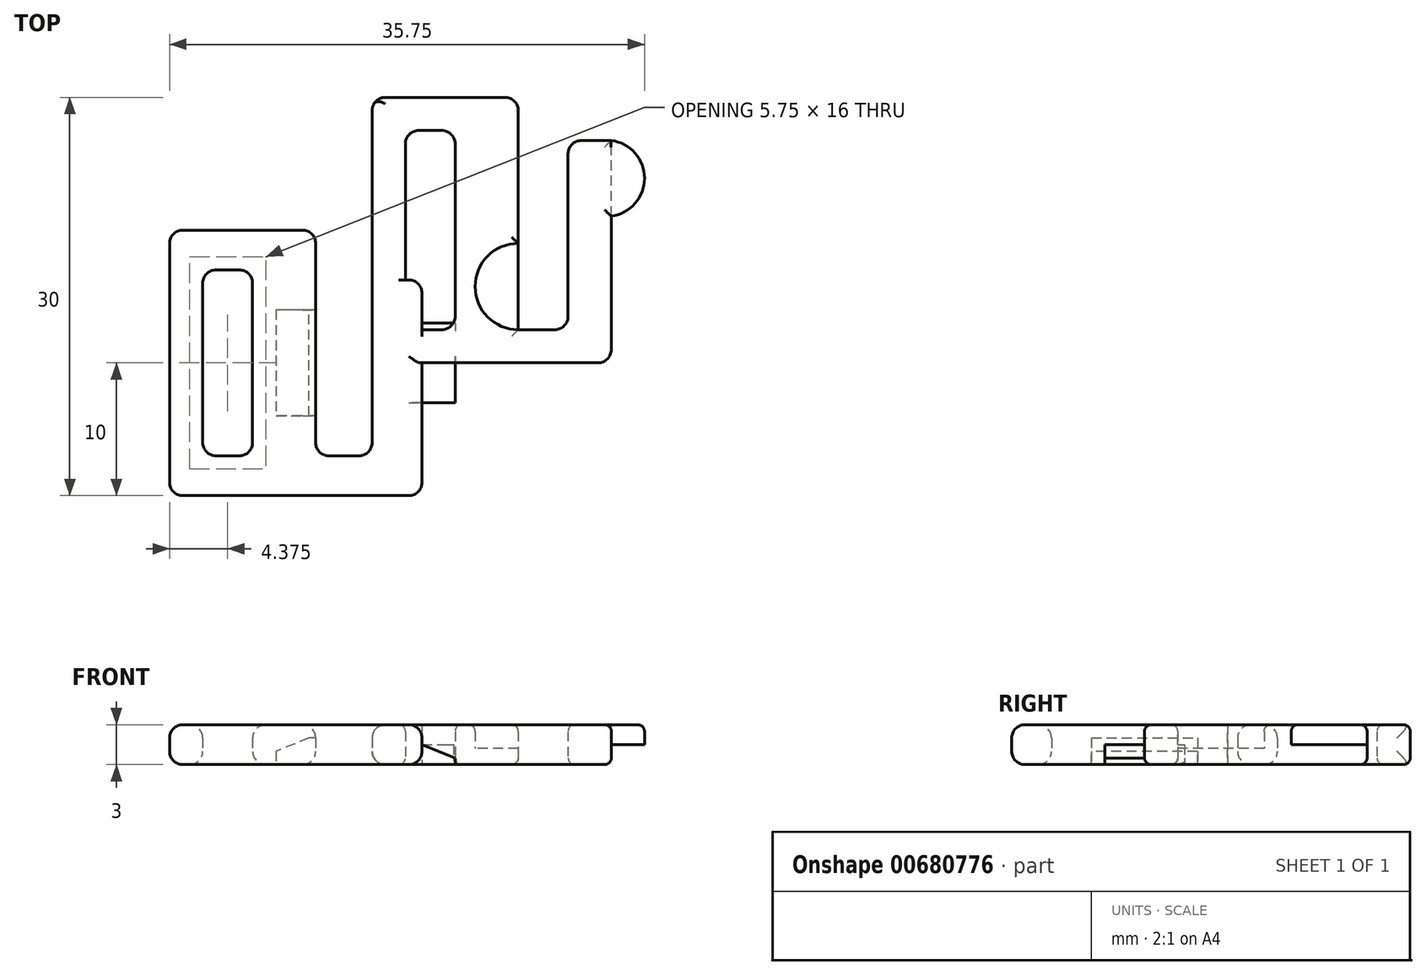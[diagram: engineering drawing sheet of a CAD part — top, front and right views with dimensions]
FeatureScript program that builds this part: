
annotation { "Feature Type Name" : "Feature", "Feature Type Description" : "" }
export const myFeature = defineFeature(function(context is Context, id is Id, definition is map)
    precondition{}
    {
        {
            var Q0;
            Q0=qCreatedBy(makeId("Top.planeOp"),FACE);
            var sketch = newSketch(context, id + "F0", { "sketchPlane" : qUnion([Q0])});
            skLineSegment(sketch, "E0.bottom", {"start": v(1, 0) * mm, "end": v(17, 0) * mm});
            skLineSegment(sketch, "E0.top", {"start": v(1, 20) * mm, "end": v(10, 20) * mm});
            skLineSegment(sketch, "E0.left", {"start": v(0, 1) * mm, "end": v(0, 19) * mm});
            skLineSegment(sketch, "E0.right", {"start": v(18, 1) * mm, "end": v(18, 11.05) * mm});
            skLineSegment(sketch, "E1.bottom", {"start": v(3.5, 17.5) * mm, "end": v(5.25, 17.5) * mm});
            skLineSegment(sketch, "E1.top", {"start": v(3.5, 2.5) * mm, "end": v(5.25, 2.5) * mm});
            skLineSegment(sketch, "E1.left", {"start": v(2.5, 16.5) * mm, "end": v(2.5, 3.5) * mm});
            skLineSegment(sketch, "E1.right", {"start": v(6.25, 16.5) * mm, "end": v(6.25, 3.5) * mm});
            skLineSegment(sketch, "E2.top", {"start": v(11, 2.5) * mm, "end": v(13.75, 2.5) * mm});
            skLineSegment(sketch, "E2.left", {"start": v(11, 19) * mm, "end": v(11, 2.5) * mm});
            skLineSegment(sketch, "E2.right", {"start": v(14.75, 15.75) * mm, "end": v(14.75, 3.5) * mm});
            skLineSegment(sketch, "E3", {"start": v(15.75, 16.75) * mm, "end": v(18, 16.75) * mm});
            skArc(sketch, "E4", {"start": v(18, 11.05) * mm, "mid": v(20.48, 14.27) * mm, "end": v(17.25, 16.75) * mm});
            skPoint(sketch, "E4.second.point", {"position": v(18, 11.05) * mm});
            skPoint(sketch, "E4.third.point", {"position": v(14.75, 13.9) * mm});
            skArc(sketch, "E5", {"start": v(11, 9) * mm, "mid": v(7.75, 5.75) * mm, "end": v(11, 2.5) * mm});
            skPoint(sketch, "E6.visualSharp", {"position": v(0, 20) * mm});
            skArc(sketch, "E6.filletArc", {"start": v(1, 20) * mm, "mid": v(0.3, 19.7) * mm, "end": v(0, 19) * mm});
            skPoint(sketch, "E7.visualSharp", {"position": v(0, 0) * mm});
            skArc(sketch, "E7.filletArc", {"start": v(0, 1) * mm, "mid": v(0.3, 0.3) * mm, "end": v(1, 0) * mm});
            skPoint(sketch, "E8.visualSharp", {"position": v(18, 0) * mm});
            skArc(sketch, "E8.filletArc", {"start": v(17, 0) * mm, "mid": v(17.7, 0.3) * mm, "end": v(18, 1) * mm});
            skPoint(sketch, "E9.visualSharp", {"position": v(11, 20) * mm});
            skArc(sketch, "E9.filletArc", {"start": v(11, 19) * mm, "mid": v(10.7, 19.7) * mm, "end": v(10, 20) * mm});
            skPoint(sketch, "E10.visualSharp", {"position": v(14.75, 2.5) * mm});
            skArc(sketch, "E10.filletArc", {"start": v(13.75, 2.5) * mm, "mid": v(14.46, 2.8) * mm, "end": v(14.75, 3.5) * mm});
            skPoint(sketch, "E11.visualSharp", {"position": v(14.75, 16.75) * mm});
            skArc(sketch, "E11.filletArc", {"start": v(15.75, 16.75) * mm, "mid": v(15.04, 16.46) * mm, "end": v(14.75, 15.75) * mm});
            skPoint(sketch, "E12.visualSharp", {"position": v(2.5, 2.5) * mm});
            skArc(sketch, "E12.filletArc", {"start": v(2.5, 3.5) * mm, "mid": v(2.8, 2.8) * mm, "end": v(3.5, 2.5) * mm});
            skPoint(sketch, "E13.visualSharp", {"position": v(2.5, 17.5) * mm});
            skArc(sketch, "E13.filletArc", {"start": v(3.5, 17.5) * mm, "mid": v(2.8, 17.2) * mm, "end": v(2.5, 16.5) * mm});
            skPoint(sketch, "E14.visualSharp", {"position": v(6.25, 17.5) * mm});
            skArc(sketch, "E14.filletArc", {"start": v(6.25, 16.5) * mm, "mid": v(5.96, 17.2) * mm, "end": v(5.25, 17.5) * mm});
            skPoint(sketch, "E15.visualSharp", {"position": v(6.25, 2.5) * mm});
            skArc(sketch, "E15.filletArc", {"start": v(5.25, 2.5) * mm, "mid": v(5.96, 2.8) * mm, "end": v(6.25, 3.5) * mm});
            skLineSegment(sketch, "E16.trimOffspring", {"start": v(14.75, 13.9) * mm, "end": v(14.75, 13.9) * mm});
            skLineSegment(sketch, "E17", {"start": v(18, 11.05) * mm, "end": v(18, 16.75) * mm});
            skSolve(sketch);
        }
        {
            var Q0;
            Q0=makeQuery(id+"F0.imprint","IMPRINT",FACE,{"disambiguationData":[TD([[makeQuery(id+"F0.imprint","IMPRINT",EDGE,{"derivedFrom":sQuery(id+"F0.wireOp",EDGE,"E0.bottom")}),1.0]])]});
            var Q1;
            {var subQ0=sQuery(id+"F0.wireOp",EDGE,"E17");Q1=makeQuery(id+"F0.imprint","IMPRINT",FACE,{"disambiguationData":[TD([[makeQuery(id+"F0.imprint","IMPRINT",EDGE,{"derivedFrom":subQ0}),-1.0]])]});}
            extrude(context, id + "F1", {"entities" : qUnion([Q0, Q1]), "depth" : 3 * mm, "offsetDistance" : 25 * mm});
        }
        {
            var Q0;
            {var subQ0=sQuery(id+"F0.wireOp",EDGE,"E5");Q0=makeQuery(id+"F0.imprint","IMPRINT",FACE,{"disambiguationData":[TD([[makeQuery(id+"F0.imprint","IMPRINT",EDGE,{"derivedFrom":subQ0}),1.0]])]});}
            extrude(context, id + "F2", {"entities" : qUnion([Q0]), "operationType" : NewBodyOperationType.ADD, "depth" : 1.2 * mm, "offsetDistance" : 25 * mm});
        }
        {
            var Q0;
            {var subQ0=sQuery(id+"F0.wireOp",EDGE,"E17");Q0=makeQuery(id+"F0.imprint","IMPRINT",FACE,{"disambiguationData":[TD([[makeQuery(id+"F0.imprint","IMPRINT",EDGE,{"derivedFrom":subQ0}),-1.0]])]});}
            extrude(context, id + "F3", {"entities" : qUnion([Q0]), "operationType" : NewBodyOperationType.REMOVE, "depth" : 1.5 * mm, "offsetDistance" : 25 * mm});
        }
        {
            var Q0;
            Q0=makeQuery(id+"F1.opExtrude","CAP_EDGE",EDGE,{"disambiguationData":[OSD([sQuery(id+"F0.wireOp",EDGE,"E0.bottom")])],"isStart":false});
            var Q1;
            Q1=makeQuery(id+"F1.opExtrude","CAP_EDGE",EDGE,{"disambiguationData":[OSD([sQuery(id+"F0.wireOp",EDGE,"E2.right")])],"isStart":false});
            var Q2;
            Q2=makeQuery(id+"F1.opExtrude","CAP_EDGE",EDGE,{"disambiguationData":[OSD([sQuery(id+"F0.wireOp",EDGE,"E4")])],"isStart":false});
            var Q3;
            Q3=makeQuery(id+"F1.opExtrude","CAP_EDGE",EDGE,{"disambiguationData":[OSD([sQuery(id+"F0.wireOp",EDGE,"E0.left")])],"isStart":true});
            var Q4;
            Q4=makeQuery(id+"F1.opExtrude","CAP_EDGE",EDGE,{"disambiguationData":[OSD([sQuery(id+"F0.wireOp",EDGE,"E11.filletArc")])],"isStart":true});
            var Q5;
            Q5=makeQuery(id+"F1.opExtrude","CAP_EDGE",EDGE,{"disambiguationData":[OSD([sQuery(id+"F0.wireOp",EDGE,"E1.left")])],"isStart":false});
            var Q6;
            Q6=makeQuery(id+"F1.opExtrude","CAP_EDGE",EDGE,{"disambiguationData":[OSD([sQuery(id+"F0.wireOp",EDGE,"E1.left")])],"isStart":true});
            fillet(context, id + "F4", {"entities" : qUnion([Q0, Q1, Q2, Q3, Q4, Q5, Q6]), "radius" : 0.5 * mm, "tangentPropagation" : true, "allowEdgeOverflow" : false});
        }
        {
            var Q0;
            Q0=qCreatedBy(makeId("Top.planeOp"),FACE);
            var sketch = newSketch(context, id + "F5", { "sketchPlane" : qUnion([Q0])});
            skLineSegment(sketch, "E18.bottom", {"start": v(-14.25, -10) * mm, "end": v(2.75, -10) * mm});
            skLineSegment(sketch, "E18.top", {"start": v(-14.25, 10) * mm, "end": v(-5.25, 10) * mm});
            skLineSegment(sketch, "E18.left", {"start": v(-15.25, -9) * mm, "end": v(-15.25, 9) * mm});
            skLineSegment(sketch, "E18.right", {"start": v(3.75, -9) * mm, "end": v(3.75, 0) * mm});
            skLineSegment(sketch, "E19.bottom", {"start": v(-11.75, 7) * mm, "end": v(-10, 7) * mm});
            skLineSegment(sketch, "E19.top", {"start": v(-11.75, -7) * mm, "end": v(-10, -7) * mm});
            skLineSegment(sketch, "E19.left", {"start": v(-12.75, 6) * mm, "end": v(-12.75, -6) * mm});
            skLineSegment(sketch, "E19.right", {"start": v(-9, 6) * mm, "end": v(-9, -6) * mm});
            skLineSegment(sketch, "E20.top", {"start": v(-3.25, -7) * mm, "end": v(-1, -7) * mm});
            skLineSegment(sketch, "E20.left", {"start": v(-4.25, 9) * mm, "end": v(-4.25, -6) * mm});
            skLineSegment(sketch, "E20.right", {"start": v(0, 5.25) * mm, "end": v(0, -6) * mm});
            skLineSegment(sketch, "E21", {"start": v(1, 6.25) * mm, "end": v(2.75, 6.25) * mm});
            skPoint(sketch, "E22.visualSharp", {"position": v(-15.25, 10) * mm});
            skArc(sketch, "E22.filletArc", {"start": v(-14.25, 10) * mm, "mid": v(-14.96, 9.7) * mm, "end": v(-15.25, 9) * mm});
            skPoint(sketch, "E23.visualSharp", {"position": v(-15.25, -10) * mm});
            skArc(sketch, "E23.filletArc", {"start": v(-15.25, -9) * mm, "mid": v(-14.96, -9.7) * mm, "end": v(-14.25, -10) * mm});
            skPoint(sketch, "E24.visualSharp", {"position": v(3.75, -10) * mm});
            skArc(sketch, "E24.filletArc", {"start": v(2.75, -10) * mm, "mid": v(3.46, -9.7) * mm, "end": v(3.75, -9) * mm});
            skPoint(sketch, "E25.visualSharp", {"position": v(-4.25, 10) * mm});
            skArc(sketch, "E25.filletArc", {"start": v(-4.25, 9) * mm, "mid": v(-4.54, 9.7) * mm, "end": v(-5.25, 10) * mm});
            skPoint(sketch, "E26.visualSharp", {"position": v(0, -7) * mm});
            skArc(sketch, "E26.filletArc", {"start": v(-1, -7) * mm, "mid": v(-0.3, -6.7) * mm, "end": v(0, -6) * mm});
            skPoint(sketch, "E27.visualSharp", {"position": v(0, 6.25) * mm});
            skArc(sketch, "E27.filletArc", {"start": v(1, 6.25) * mm, "mid": v(0.3, 5.96) * mm, "end": v(0, 5.25) * mm});
            skPoint(sketch, "E28.visualSharp", {"position": v(-12.75, -7) * mm});
            skArc(sketch, "E28.filletArc", {"start": v(-12.75, -6) * mm, "mid": v(-12.46, -6.7) * mm, "end": v(-11.75, -7) * mm});
            skPoint(sketch, "E29.visualSharp", {"position": v(-12.75, 7) * mm});
            skArc(sketch, "E29.filletArc", {"start": v(-11.75, 7) * mm, "mid": v(-12.46, 6.7) * mm, "end": v(-12.75, 6) * mm});
            skPoint(sketch, "E30.visualSharp", {"position": v(-9, 7) * mm});
            skArc(sketch, "E30.filletArc", {"start": v(-9, 6) * mm, "mid": v(-9.3, 6.7) * mm, "end": v(-10, 7) * mm});
            skPoint(sketch, "E31.visualSharp", {"position": v(-9, -7) * mm});
            skArc(sketch, "E31.filletArc", {"start": v(-10, -7) * mm, "mid": v(-9.3, -6.7) * mm, "end": v(-9, -6) * mm});
            skLineSegment(sketch, "E32", {"start": v(3.75, 0) * mm, "end": v(3.75, 5.25) * mm});
            skPoint(sketch, "E33.visualSharp", {"position": v(3.75, 6.25) * mm});
            skArc(sketch, "E33.filletArc", {"start": v(3.75, 5.25) * mm, "mid": v(3.46, 5.96) * mm, "end": v(2.75, 6.25) * mm});
            skPoint(sketch, "E34.visualSharp", {"position": v(-4.25, -7) * mm});
            skArc(sketch, "E34.filletArc", {"start": v(-4.25, -6) * mm, "mid": v(-3.96, -6.7) * mm, "end": v(-3.25, -7) * mm});
            skLineSegment(sketch, "E35.bottom", {"start": v(-4.25, 4) * mm, "end": v(-7.25, 4) * mm});
            skLineSegment(sketch, "E35.top", {"start": v(-4.25, -4) * mm, "end": v(-7.25, -4) * mm});
            skLineSegment(sketch, "E35.left", {"start": v(-4.25, 4) * mm, "end": v(-4.25, -4) * mm});
            skLineSegment(sketch, "E35.right", {"start": v(-7.25, 4) * mm, "end": v(-7.25, -4) * mm});
            skLineSegment(sketch, "E36.bottom", {"start": v(3.75, 4) * mm, "end": v(6.25, 4) * mm});
            skLineSegment(sketch, "E36.top", {"start": v(3.75, -4) * mm, "end": v(6.25, -4) * mm});
            skLineSegment(sketch, "E36.left", {"start": v(3.75, 4) * mm, "end": v(3.75, -4) * mm});
            skLineSegment(sketch, "E36.right", {"start": v(6.25, 4) * mm, "end": v(6.25, -4) * mm});
            skLineSegment(sketch, "E37.0", {"start": v(3.75, 3) * mm, "end": v(6.25, 3) * mm});
            skLineSegment(sketch, "E38.0", {"start": v(3.75, -3) * mm, "end": v(6.25, -3) * mm});
            skSolve(sketch);
        }
        {
            var Q0;
            Q0=makeQuery(id+"F5.imprint","IMPRINT",FACE,{"disambiguationData":[TD([[makeQuery(id+"F5.imprint","IMPRINT",EDGE,{"derivedFrom":sQuery(id+"F5.wireOp",EDGE,"E18.bottom")}),1.0]])]});
            var Q1;
            Q1=makeQuery(id+"F5.imprint","IMPRINT",FACE,{"disambiguationData":[TD([[makeQuery(id+"F5.imprint","IMPRINT",EDGE,{"derivedFrom":sQuery(id+"F5.wireOp",EDGE,"E35.bottom")}),1.0]])]});
            extrude(context, id + "F6", {"entities" : qUnion([Q0, Q1]), "depth" : 3 * mm, "offsetDistance" : 25 * mm});
        }
        {
            var Q0;
            {var subQ0=sQuery(id+"F5.wireOp",EDGE,"E37.0");Q0=makeQuery(id+"F5.imprint","IMPRINT",FACE,{"disambiguationData":[TD([[makeQuery(id+"F5.imprint","IMPRINT",EDGE,{"derivedFrom":subQ0}),-1.0]])]});}
            extrude(context, id + "F7", {"entities" : qUnion([Q0]), "operationType" : NewBodyOperationType.ADD, "depth" : 1.5 * mm, "offsetDistance" : 25 * mm});
        }
        {
            var Q0;
            Q0=makeQuery(id+"F7.opExtrude","CAP_EDGE",EDGE,{"disambiguationData":[OSD([sQuery(id+"F5.wireOp",EDGE,"E36.right")])],"isStart":false});
            chamfer(context, id + "F8", {"entities" : qUnion([Q0]), "chamferType" : ChamferType.TWO_OFFSETS, "width1" : 1 * mm, "oppositeDirection" : false, "width2" : 2.5 * mm, "tangentPropagation" : true});
        }
        {
            var Q0;
            Q0=makeQuery(id+"F5.imprint","IMPRINT",FACE,{"disambiguationData":[TD([[makeQuery(id+"F5.imprint","IMPRINT",EDGE,{"derivedFrom":sQuery(id+"F5.wireOp",EDGE,"E35.bottom")}),1.0]])]});
            extrude(context, id + "F9", {"entities" : qUnion([Q0]), "operationType" : NewBodyOperationType.REMOVE, "depth" : 2 * mm, "offsetDistance" : 25 * mm});
        }
        {
            var Q0;
            Q0=makeQuery(id+"F9.boolean.opBoolean","COPY",EDGE,{"derivedFrom":makeQuery(id+"F9.opExtrude","CAP_EDGE",EDGE,{"disambiguationData":[OSD([sQuery(id+"F5.wireOp",EDGE,"E35.right")])],"isStart":false})});
            chamfer(context, id + "F10", {"entities" : qUnion([Q0]), "chamferType" : ChamferType.TWO_OFFSETS, "width1" : 1 * mm, "oppositeDirection" : false, "width2" : 2.5 * mm, "tangentPropagation" : true});
        }
        {
            var Q0;
            Q0=makeQuery(id+"F6.opExtrude","CAP_EDGE",EDGE,{"disambiguationData":[OSD([sQuery(id+"F5.wireOp",EDGE,"E19.bottom")])],"isStart":false});
            var Q1;
            Q1=makeQuery(id+"F6.opExtrude","CAP_EDGE",EDGE,{"disambiguationData":[OSD([sQuery(id+"F5.wireOp",EDGE,"E19.bottom")])],"isStart":true});
            var Q2;
            Q2=makeQuery(id+"F6.opExtrude","CAP_EDGE",EDGE,{"disambiguationData":[OSD([sQuery(id+"F5.wireOp",EDGE,"E18.top")])],"isStart":false});
            var Q3;
            Q3=makeQuery(id+"F6.opExtrude","CAP_EDGE",EDGE,{"disambiguationData":[OSD([sQuery(id+"F5.wireOp",EDGE,"E18.bottom")])],"isStart":true});
            var Q4;
            {var subQ1=sQuery(id+"F5.wireOp",EDGE,"E34.filletArc");var subQ2=sQuery(id+"F5.wireOp",EDGE,"E35.left");var subQ3=sQuery(id+"F5.wireOp",EDGE,"E20.left");Q4=makeQuery(id+"F9.boolean.opBoolean","SPLIT",EDGE,{"disambiguationData":[TD([makeQuery(id+"F6.opExtrude","SWEPT_FACE",FACE,{"disambiguationData":[OSD([subQ1])]})])],"derivedFrom":makeQuery(id+"F6.opExtrude","CAP_EDGE",EDGE,{"disambiguationData":[OSD([subQ3,subQ2])],"isStart":true})});}
            fillet(context, id + "F11", {"entities" : qUnion([Q0, Q1, Q2, Q3, Q4]), "radius" : 1 * mm, "tangentPropagation" : true, "allowEdgeOverflow" : false});
        }
    });
